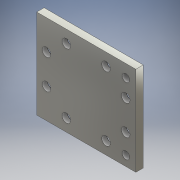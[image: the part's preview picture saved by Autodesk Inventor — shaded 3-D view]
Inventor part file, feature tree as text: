
AUTODESK INVENTOR PART (.ipt)
format: ipt  version: 2017 (Build 210142000, 142)  size: 215,040 bytes
history: native  units: mm
features: extrude x3, sketch x3, projected_geometry x1
ambient origin geometry x8: Origin, YZ Plane, XZ Plane, XY Plane, X Axis, Y Axis, Z Axis, Center Point
bodies: Solid1 (feature_tree)
feature tree (7):
  extrude  "Extrusion1"  Depth=3.0mm TaperAngle=0.0deg
  extrude  "Extrusion2"  Depth=3.0mm TaperAngle=0.0deg
  extrude  "Extrusion4"  TaperAngle=0.0deg  [1 undecoded]
  sketch  "Sketch1"  dims[d0=40.0mm d1=36.0mm d2=3.0mm d3=0.0mm]
  sketch  "Sketch2"  dims[d4=4.0mm d5=12.0mm d6=12.0mm d7=6.0mm d8=6.0mm d9=3.0mm d10=0.0mm]
  sketch  "Sketch5"  dims[d11=6.0mm d13=0.0mm d14=0.0mm d15=5.0mm d16=4.0mm d17=4.0mm d18=12.0mm d19=4.0mm d20=24.0mm d21=12.0mm d22=5.0mm d23=12.0mm d24=31.0mm d25=28.0mm d26=5.0mm d27=28.0mm d29=36.0mm d30=36.0mm d31=5.0mm d32=36.0mm d34=5.0mm d35=0.0mm d36=35.939652mm d37=4.060348mm d38=35.939652mm d39=3.5mm d40=0.0mm d41=0.0mm d42=3.5mm d43=0.0mm d44=0.0mm d45=6.0mm d46=3.5mm d47=0.0mm d48=0.0mm d49=6.0mm d50=3.5mm d51=0.0mm d52=0.0mm d53=6.0mm d54=3.5mm d55=0.0mm d56=0.0mm d57=6.0mm d58=3.5mm d59=0.0mm d60=0.0mm d61=6.0mm d62=3.5mm d63=0.0mm d64=0.0mm d65=6.0mm d66=3.5mm d67=0.0mm d68=0.0mm d69=6.0mm d72=2.0mm d73=0.0mm d74=68.0mm d75=67.0mm d76=68.0mm d77=67.0mm d78=68.0mm d79=67.0mm d80=75.939652mm d81=60.0mm d88=27.0mm d89=3.0mm d90=31.0mm]
  projected_geometry  "Projected Loop1"
note: 1 required parameter value undecoded (feature->parameter linkage not recoverable at this tier; creation-order binding heuristic only, values carry confidence <= 0.55)
